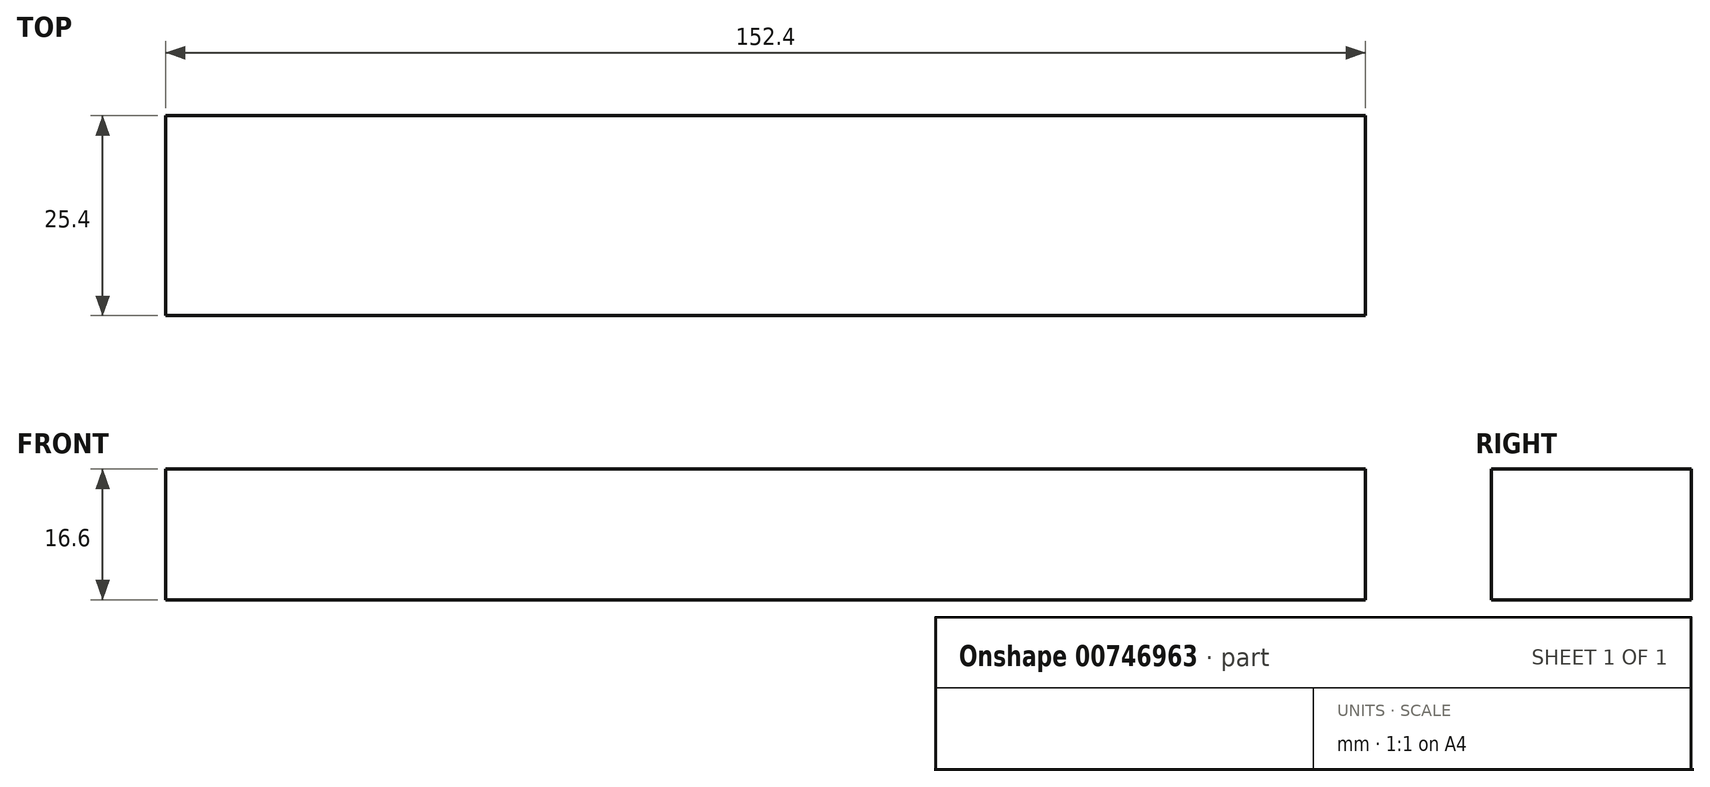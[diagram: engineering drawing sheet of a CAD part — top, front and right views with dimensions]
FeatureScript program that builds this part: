
annotation { "Feature Type Name" : "Feature", "Feature Type Description" : "" }
export const myFeature = defineFeature(function(context is Context, id is Id, definition is map)
    precondition{}
    {
        {
            var Q0;
            Q0=qCreatedBy(makeId("Front.planeOp"),FACE);
            var sketch = newSketch(context, id + "F0", { "sketchPlane" : qUnion([Q0])});
            skLineSegment(sketch, "E0.bottom", {"start": v(76.2, 8.3) * mm, "end": v(-76.2, 8.3) * mm});
            skLineSegment(sketch, "E0.top", {"start": v(76.2, -8.3) * mm, "end": v(-76.2, -8.3) * mm});
            skLineSegment(sketch, "E0.left", {"start": v(76.2, 8.3) * mm, "end": v(76.2, -8.3) * mm});
            skLineSegment(sketch, "E0.right", {"start": v(-76.2, 8.3) * mm, "end": v(-76.2, -8.3) * mm});
            skPoint(sketch, "E0.middle", {"position": v(0, 0) * mm});
            skSolve(sketch);
        }
        {
            var Q0;
            Q0=makeQuery(id+"F0.imprint","IMPRINT",FACE,{"disambiguationData":[TD([[makeQuery(id+"F0.imprint","IMPRINT",EDGE,{"derivedFrom":sQuery(id+"F0.wireOp",EDGE,"E0.bottom")}),1.0]])]});
            extrude(context, id + "F1", {"entities" : qUnion([Q0]), "depth" : 25.4 * mm, "offsetDistance" : 25.4 * mm});
        }
    });
